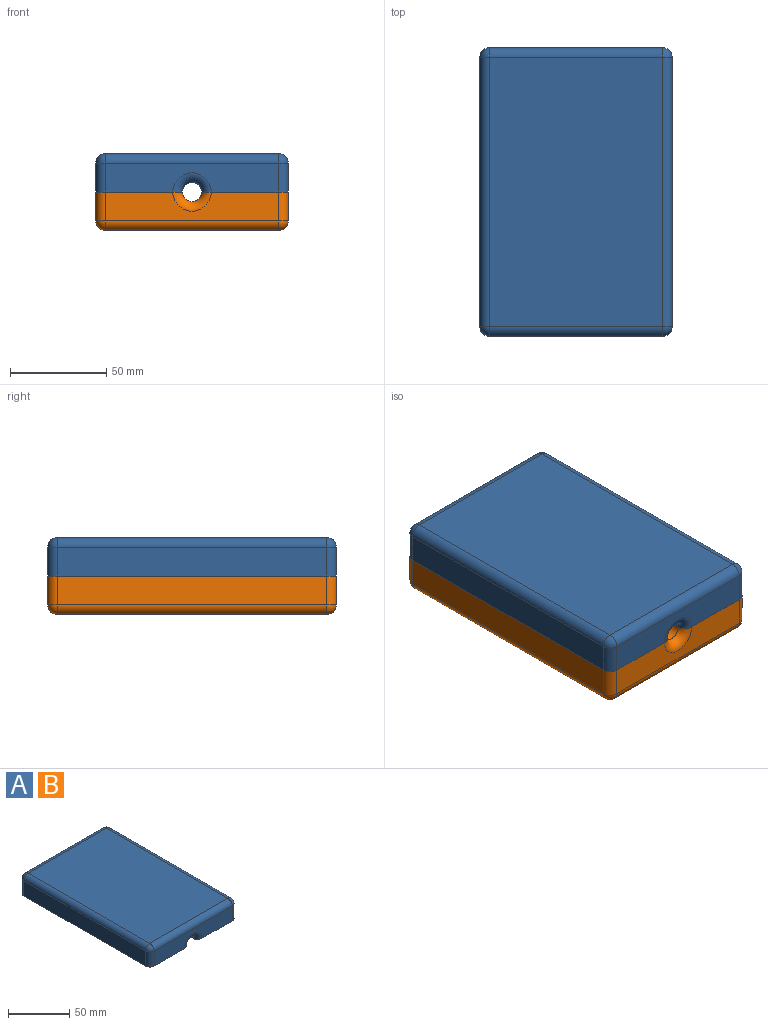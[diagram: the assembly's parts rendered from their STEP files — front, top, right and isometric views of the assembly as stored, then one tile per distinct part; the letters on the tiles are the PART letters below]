
ASSEMBLY  parts=2 mates=1
PART A: 30 faces, bbox 100x150x20 mm
  f0: plane 90x15mm, normal (0,1,0), area 1192.9mm2, adj f2,f6,f12,f16,f18,f27
  f1: plane 90x15mm, normal (0,-1,0), area 1192.9mm2, adj f2,f6,f7,f9,f10,f28
  f2: plane 150x45mm, normal (0,0,-1), area 6689.3mm2, adj f0,f1,f4,f7,f12,f21,f25,f27
  f3: plane 140x15mm, normal (1,0,0), area 2100mm2, adj f6,f9,f15,f18
  f4: plane 140x15mm, normal (-1,0,0), area 2100mm2, adj f2,f7,f11,f12
  f5: plane 140x90mm, normal (0,0,1), area 12600mm2, adj f10,f11,f15,f16
  f6: plane 150x45mm, normal (0,0,-1), area 6689.3mm2, adj f0,f1,f3,f9,f18,f19,f23,f27
  f7: cylinder r=5mm len=15mm, axis (0,0,-1), area 117.8mm2, adj f1,f2,f4,f8
  f8: sphere r=5mm, area 39.3mm2, adj f7,f10,f11
  f9: cylinder r=5mm len=15mm, axis (0,0,1), area 117.8mm2, adj f1,f3,f6,f13
  f10: cylinder r=5mm len=90mm, axis (-1,0,0), area 706.9mm2, adj f1,f5,f8,f13
  f11: cylinder r=5mm len=140mm, axis (0,1,0), area 1099.6mm2, adj f4,f5,f8,f14
  f12: cylinder r=5mm len=15mm, axis (0,0,1), area 117.8mm2, adj f0,f2,f4,f14
  f13: sphere r=5mm, area 39.3mm2, adj f9,f10,f15
  f14: sphere r=5mm, area 39.3mm2, adj f11,f12,f16
  f15: cylinder r=5mm len=140mm, axis (0,-1,0), area 1099.6mm2, adj f3,f5,f13,f17
  f16: cylinder r=5mm len=90mm, axis (1,0,0), area 706.9mm2, adj f0,f5,f14,f17
  f17: sphere r=5mm, area 39.3mm2, adj f15,f16,f18
  f18: cylinder r=5mm len=15mm, axis (0,0,-1), area 117.8mm2, adj f0,f3,f6,f17
  f19: cylinder r=2.5mm len=12mm, axis (0,0,-1), area 188.5mm2, adj f6,f20
  f20: cone r=0mm half-angle=59deg, axis (0,0,-1), area 22.9mm2, adj f19
  f21: cylinder r=2.5mm len=12mm, axis (0,0,-1), area 188.5mm2, adj f2,f22
  f22: cone r=0mm half-angle=59deg, axis (0,0,-1), area 22.9mm2, adj f21
  f23: cylinder r=2.5mm len=12mm, axis (0,0,-1), area 188.5mm2, adj f6,f24
  f24: cone r=0mm half-angle=59deg, axis (0,0,-1), area 22.9mm2, adj f23
  f25: cylinder r=2.5mm len=12mm, axis (0,0,-1), area 188.5mm2, adj f2,f26
  f26: cone r=0mm half-angle=59deg, axis (0,0,-1), area 22.9mm2, adj f25
  f27: torus R=10mm, axis (0,-1,0), area 168.2mm2, adj f0,f2,f6,f29
  f28: torus R=10mm, axis (0,-1,0), area 168.2mm2, adj f1,f2,f6,f29
  f29: cylinder r=5mm len=140mm, axis (0,1,0), area 2199.1mm2, adj f2,f6,f27,f28
PART B: same geometry as A
PLACE A t=(100.67,35.87,-33.38)mm
PLACE B rot(axis=(0,1,0),180deg) t=(100.67,35.87,-33.38)mm
MATE fastened B.f21 <-> A.f19  axis (0,0,1) through (140.67,100.87,-33.38)mm
